# Revit family: SE-SU-300_GENERADO
name_source: partatom
category: Equipos mecánicos
revit_build: Autodesk Revit 2014 (Build: 20130308_1515(x64)
units: mm (PartAtom-declared; Revit-internal decimal feet)

## types (20) — shared parameters
Depth = 465 mm  [stored 1.52559 ft]
Fabricante = SAMMIC S.L.
Foodservice Equipment Identifier = Sí
Revision Code = 1
URL = https://www.sammic.com
Width = 384 mm  [stored 1.25984 ft]

## per-type parameters (varying)
| type | Comentarios de tipo | Cycle | FL Amps | Height | Modelo | Specification by Manufacturer | URL Cutsheet | Volts | Weight in Pounds |
| Vacuum packing machine SE-306 230/50-60/1 | Tabletop model. 6 m³/h. 320 mm. | 50 Hz | 3 A | 405 mm  [stored 1.32874 ft] | 1140626 | 320 mm. sealing bar.
6 m³/h Busch vacuum pump.
Vacuum controlled by sensor. | http://www.sammic.com | 230 V | 75 |
| Vacuum packing machine SE-306 120/60/1 | Tabletop model. 6 m³/h. 320 mm. | 60 Hz | 6 A | 405 mm  [stored 1.32874 ft] | 1140627 | 320 mm. sealing bar.
6 m³/h Busch vacuum pump.
Vacuum controlled by sensor. | http://www.sammic.com | 120 V | 75 |
| Vacuum packing machine SE-306 230/50-60/1 KSA | Tabletop model. 6 m³/h. 320 mm. | 50 Hz | 3 A | 405 mm  [stored 1.32874 ft] | 1140647 | 320 mm. sealing bar.
6 m³/h Busch vacuum pump.
Vacuum controlled by sensor. |  | 230 V | 75 |
| Vacuum packing machine SE-310 230/50-60/1 | Tabletop model. 10 m³/h. 320 mm. | 50 Hz | 3 A | 403 mm  [stored 1.32218 ft] | 1140628 | 320 mm. sealing bar.
10 m³/h Busch vacuum pump.
Vacuum controlled by sensor. | http://www.sammic.com | 230 V | 75 |
| Vacuum packing machine SE-310 120/50-60/1 | Tabletop model. 10 m³/h. 320 mm. | 60 Hz | 6 A | 403 mm  [stored 1.32218 ft] | 1140629 | 320 mm. sealing bar.
10 m³/h Busch vacuum pump.
Vacuum controlled by sensor. | http://www.sammic.com | 120 V | 75 |
| Vacuum packing machine SE-310 230/50-60/1 KSA | Tabletop model. 10 m³/h. 320 mm. | 50 Hz | 3 A | 403 mm  [stored 1.32218 ft] | 1140645 | 320 mm. sealing bar.
10 m³/h Busch vacuum pump.
Vacuum controlled by sensor. |  | 230 V | 75 |
| Vacuum packing machine SE-316 230/50-60/1 | Tabletop model. 16 m³/h. 320 mm. | 50 Hz | 4 A | 403 mm  [stored 1.32218 ft] | 1140630 | 320 mm. sealing bar.
16 m³/h Busch vacuum pump.
Vacuum controlled by sensor. | http://www.sammic.com | 230 V | 77.2 |
| Vacuum packing machine SE-316 120/50-60/1 | Tabletop model. 16 m³/h. 320 mm. | 60 Hz | 8 A | 403 mm  [stored 1.32218 ft] | 1140631 | 320 mm. sealing bar.
16 m³/h Busch vacuum pump.
Vacuum controlled by sensor. | http://www.sammic.com | 120 V | 77.2 |
| Vacuum packing machine SU-310 230/50-60/1 | Tabletop model. 10 m³/h. 320 mm. | 50 Hz | 3 A | 403 mm  [stored 1.32218 ft] | 1140730 | 320 mm. sealing bar.
10 m³/h Busch vacuum pump.
Vacuum controlled by sensor. | http://www.sammic.com | 230 V | 75 |
| Vacuum packing machine SU-310P 230/50-60/1 | Tabletop model. 10 m³/h. 320 mm. | 50 Hz | 3 A | 403 mm  [stored 1.32218 ft] | 1140732 | 320 mm. sealing bar.
10 m³/h Busch vacuum pump.
Vacuum controlled by sensor. | http://www.sammic.com | 230 V | 75 |
| Vacuum packing machine SU-310 120/50-60/1 | Tabletop model. 10 m³/h. 320 mm. | 60 Hz | 6 A | 403 mm  [stored 1.32218 ft] | 1140735 | 320 mm. sealing bar.
10 m³/h Busch vacuum pump.
Vacuum controlled by sensor. | http://www.sammic.com | 120 V | 75 |
| Vacuum packing machine SU-310P 120/50-60/1 | Tabletop model. 10 m³/h. 320 mm. | 60 Hz | 6 A | 403 mm  [stored 1.32218 ft] | 1140737 | 320 mm. sealing bar.
10 m³/h Busch vacuum pump.
Vacuum controlled by sensor. | http://www.sammic.com | 120 V | 75 |
| Vacuum packing machine SU-316 230/50-60/1 | Tabletop model. 16 m³/h. 320 mm. | 50 Hz | 4 A | 403 mm  [stored 1.32218 ft] | 1140742 | 320 mm. sealing bar.
16 m³/h Busch vacuum pump.
Vacuum controlled by sensor. | http://www.sammic.com | 230 V | 75 |
| Vacuum packing machine SU-316P 230/50-60/1 | Tabletop model. 16 m³/h. 320 mm. | 50 Hz | 4 A | 403 mm  [stored 1.32218 ft] | 1140744 | 320 mm. sealing bar.
16 m³/h Busch vacuum pump.
Vacuum controlled by sensor. | http://www.sammic.com | 230 V | 75 |
| Vacuum packing machine SU-316+ 230/50-60/1 | Tabletop model. 16 m³/h. 320 mm. | 50 Hz | 4 A | 403 mm  [stored 1.32218 ft] | 1140745 | 320 mm. sealing bar.
16 m³/h Busch vacuum pump.
Vacuum controlled by sensor. | http://www.sammic.com | 230 V | 75 |
| Vacuum packing machine SU-316P+ 230/50-60/1 | Tabletop model. 16 m³/h. 320 mm. | 50 Hz | 4 A | 403 mm  [stored 1.32218 ft] | 1140746 | 320 mm. sealing bar.
16 m³/h Busch vacuum pump.
Vacuum controlled by sensor. | http://www.sammic.com | 230 V | 75 |
| Vacuum packing machine SU-316 120/50-60/1 | Tabletop model. 16 m³/h. 320 mm. | 60 Hz | 8 A | 403 mm  [stored 1.32218 ft] | 1140751 | 320 mm. sealing bar.
16 m³/h Busch vacuum pump.
Vacuum controlled by sensor. | http://www.sammic.com | 120 V | 75 |
| Vacuum packing machine SU-316P 120/50-60/1 | Tabletop model. 16 m³/h. 320 mm. | 60 Hz | 8 A | 403 mm  [stored 1.32218 ft] | 1140753 | 320 mm. sealing bar.
16 m³/h Busch vacuum pump.
Vacuum controlled by sensor. | http://www.sammic.com | 120 V | 75 |
| Vacuum packing machine SU-316+ 120/50-60/1 | Tabletop model. 16 m³/h. 320 mm. | 60 Hz | 8 A | 403 mm  [stored 1.32218 ft] | 1140754 | 320 mm. sealing bar.
16 m³/h Busch vacuum pump.
Vacuum controlled by sensor. | http://www.sammic.com | 120 V | 75 |
| Vacuum packing machine SU-316P+ 120/50-60/1 (with PLUS welding option) | Tabletop model. 16 m³/h. 320 mm. | 60 Hz | 8 A | 403 mm  [stored 1.32218 ft] | 1140755 | 320 mm. sealing bar.
16 m³/h Busch vacuum pump.
Vacuum controlled by sensor. | http://www.sammic.com | 120 V | 75 |

note: column(s) folded — value = type name in every type: Descripción

note: [stored X ft] marks values corroborated as IEEE doubles in the binary element streams (Revit-internal decimal feet)
